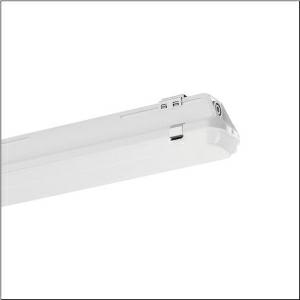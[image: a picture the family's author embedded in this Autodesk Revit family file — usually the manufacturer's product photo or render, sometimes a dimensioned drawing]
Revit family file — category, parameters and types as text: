
# Revit family: monsun_21_51fb10ml460k
name_source: partatom
category: Lighting Fixtures
units: mm (PartAtom-declared; Revit-internal decimal feet)

## family parameters
Cut with Voids When Loaded = No
Host = Face
Light Source = No
Part Type = Normal
Room Calculation Point = No
Round Connector Dimension = Use Diameter
Shared = No

## types (1)
- --- (1 x LED, 6010 lm, 33.2 W, 4000K)
    Apparent Load = 33 VA
    CIE Flux Codes = 46 76 93 94 100
    Color Rendering = 80
    Color Temperature = 4000K
    Default Elevation = 1800 mm
    Description = Monsun 21, damp-proof luminaire, chain hanger, primary optical cover: enclosure, of PMMA, light emission: direct distribution, primary light characteristic: symmetric, installation type: suspended mounting, surface-mounted, horizontal mounting, vertical mounting, LED, rated luminous flux: 6.010lm, luminous efficacy: 181lm/W, light colour: 840, colour temperature: 4000K, control gear: ON/OFF Multilumen, with terminal, 3-pole, max. 2.5mm², mains connection: 220..240V, AC, 50/60Hz, rated input power: 33W, housing, of glass-fibre reinforced plastic, uncoated, bright grey, incl. chain hanger, length: 1.299mm, width: 90mm, height: 88mm, clip for enclosure, of stainless steel (V2A), ceiling mounting element, of stainless steel (V2A), chain hanger, of stainless steel (V2A), protection rating (complete): IP66, insulation class (complete): insulation class I (protective earthing), certification: CE, ENEC, VDE, UKCA, protection symbol: D, impact resistance: IK04, permissible operating ambient temperature: -25..+35°C, standard: EN 50419, EN 60598-2-1, corresponds to IFS (International Featured Standards) requirements for safety and quality in the food industry, for indoor or canopied outdoor use, no direct snow, no direct sun, no direct rain, LABS conformity tested according to VDMA 24364:2018-05, contact your sales advisor before using the luminaires in applications with unclear chemical exposure, large temperature fluctuations or condensation-forming humidity, packaging unit: 1 piece
    Height = 88 mm
    Lamp = 1 x LED
    Lamp Light Flux = 6010 lm
    Lamp Power = 33.2 W
    Lamp count = 1
    Length = 1299 mm
    Luminous efficacy = 181 lm/W
    Manufacturer = Siteco
    ModVariant = No
    Model = 51FB10ML460K
    Mounting Place = Ceiling
    Mounting Type = Surface mounted
    Number of Poles = 1
    OnlyDefault = Yes
    Power Factor = 1
    Product Name = Monsun 21
    Product group = damp-proof luminaire
    ProductGroupID = 300
    Protection Class = Protection class I
    Protection Degree = IP 66
    RLX_Detail_Level = 1
    RLX_Emergency_Light_Flux = 0 lm
    RLX_Emergency_Type = 0
    RLX_Emergency_Type_DB = No
    RlxData = <blob elided: 90933 chars, md5=282599a7>
    Socket = socket
    Standby Power = 0 W
    System Light Flux = 6010 lm
    System Power = 33 W
    Type Comments = factory setting: luminous flux: 100 % | (A | C | E) | 77 mA
    Type Image = l_1319656.jpg
    URL = http://relux.com
    VarID = @adj_049617
    Voltage = 0 V
    Weight = 0.00 kg
    Width = 90 mm

## geometry (parser evidence)
native form markers: Blend x4, Sweep x12
no freeform markers — native parametric forms only
